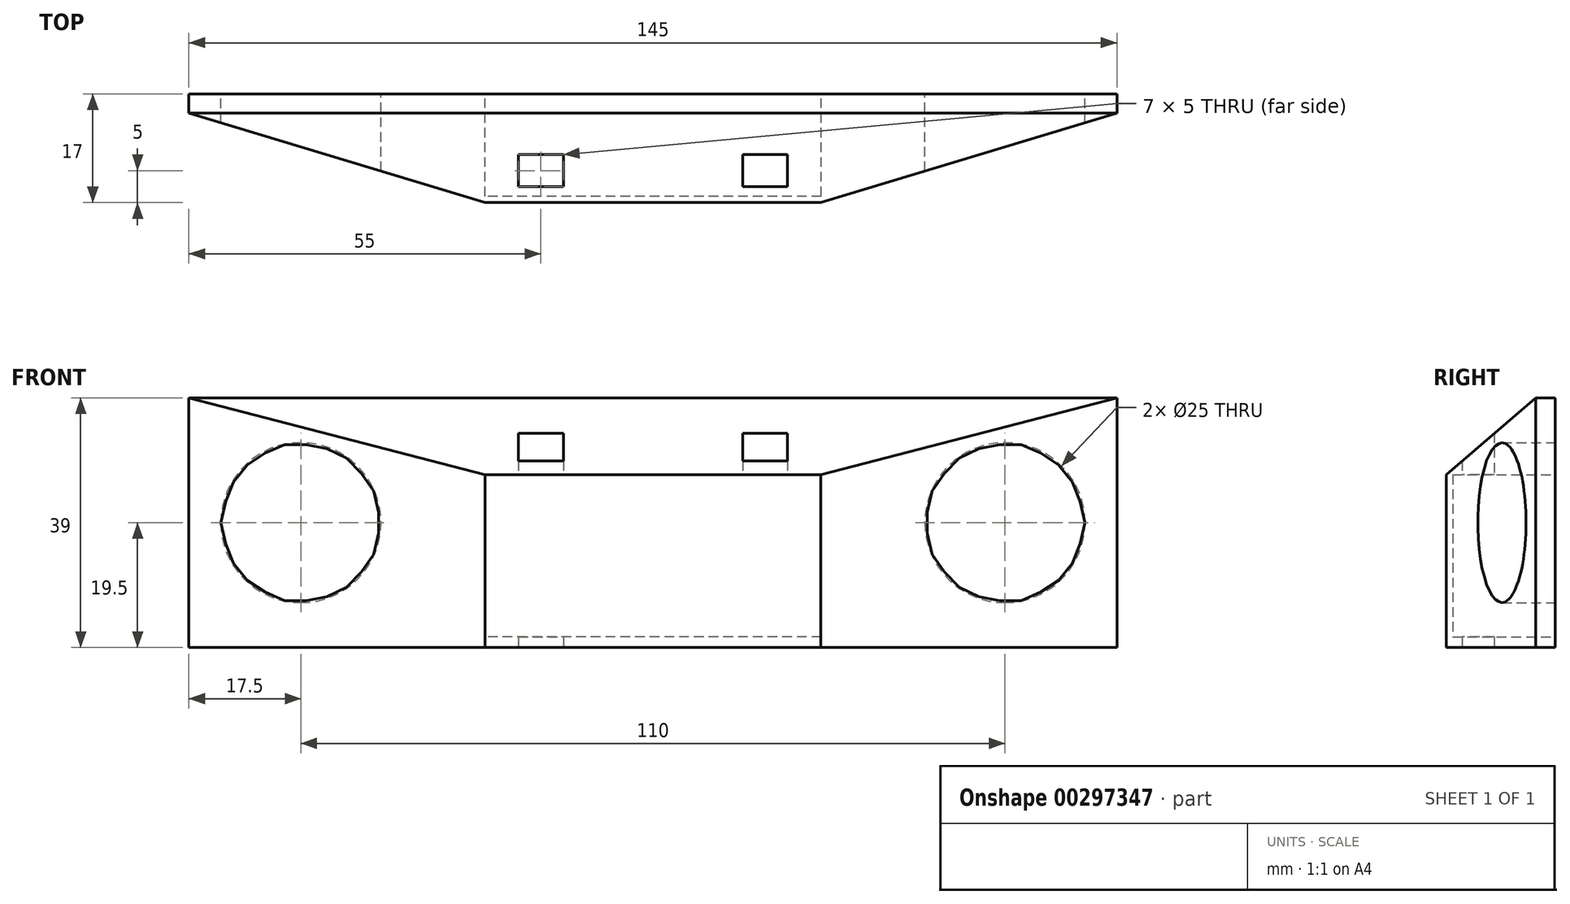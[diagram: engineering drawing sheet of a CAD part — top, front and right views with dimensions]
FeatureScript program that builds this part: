
annotation { "Feature Type Name" : "Feature", "Feature Type Description" : "" }
export const myFeature = defineFeature(function(context is Context, id is Id, definition is map)
    precondition{}
    {
        {
            var Q0;
            Q0=qCreatedBy(makeId("Front.planeOp"),FACE);
            var sketch = newSketch(context, id + "F0", { "sketchPlane" : qUnion([Q0])});
            skLineSegment(sketch, "E0.bottom", {"start": v(72.5, 19.5) * mm, "end": v(-72.5, 19.5) * mm});
            skLineSegment(sketch, "E0.top", {"start": v(72.5, -19.5) * mm, "end": v(-72.5, -19.5) * mm});
            skLineSegment(sketch, "E0.left", {"start": v(72.5, 19.5) * mm, "end": v(72.5, -19.5) * mm});
            skLineSegment(sketch, "E0.right", {"start": v(-72.5, 19.5) * mm, "end": v(-72.5, -19.5) * mm});
            skPoint(sketch, "E0.middle", {"position": v(0, 0) * mm});
            skCircle(sketch, "E1", {"center": v(-55, 0) * mm, "radius": 12.5 * mm});
            skCircle(sketch, "E2", {"center": v(55, 0) * mm, "radius": 12.5 * mm});
            skSolve(sketch);
        }
        {
            var Q0;
            Q0 = qSketchRegion(id + "F0", true);
            extrude(context, id + "F1", {"entities" : qUnion([Q0]), "depth" : 17 * mm});
        }
        {
            var Q0;
            Q0=makeQuery(id+"F1.opExtrude","CAP_FACE",FACE,{"disambiguationData":[OSD([sQuery(id+"F0.wireOp",EDGE,"E0.bottom"),sQuery(id+"F0.wireOp",EDGE,"E0.top"),sQuery(id+"F0.wireOp",EDGE,"E0.left"),sQuery(id+"F0.wireOp",EDGE,"E0.right"),sQuery(id+"F0.wireOp",EDGE,"E1"),sQuery(id+"F0.wireOp",EDGE,"E2")])],"isStart":false});
            var sketch = newSketch(context, id + "F2", { "sketchPlane" : qUnion([Q0])});
            skLineSegment(sketch, "E3.bottom", {"start": v(-26.25, -19.5) * mm, "end": v(26.25, -19.5) * mm, "construction": true});
            skLineSegment(sketch, "E3.top", {"start": v(-26.25, 7.5) * mm, "end": v(26.25, 7.5) * mm, "construction": true});
            skLineSegment(sketch, "E3.left", {"start": v(-26.25, -19.5) * mm, "end": v(-26.25, 7.5) * mm, "construction": true});
            skLineSegment(sketch, "E3.right", {"start": v(26.25, -19.5) * mm, "end": v(26.25, 7.5) * mm, "construction": true});
            skSolve(sketch);
        }
        {
            var Q0;
            Q0=makeQuery(id+"F1.opExtrude","SWEPT_FACE",FACE,{"disambiguationData":[OSD([sQuery(id+"F0.wireOp",EDGE,"E0.right")])]});
            var sketch = newSketch(context, id + "F3", { "sketchPlane" : qUnion([Q0])});
            skLineSegment(sketch, "E4", {"start": v(17, 7.5) * mm, "end": v(3, 19.5) * mm});
            skLineSegment(sketch, "E5", {"start": v(3, 19.5) * mm, "end": v(17, 19.5) * mm});
            skLineSegment(sketch, "E6", {"start": v(17, 19.5) * mm, "end": v(17, 7.5) * mm});
            skSolve(sketch);
        }
        {
            var Q0;
            Q0 = qSketchRegion(id + "F3", true);
            extrude(context, id + "F4", {"entities" : qUnion([Q0]), "operationType" : NewBodyOperationType.REMOVE, "oppositeDirection" : true, "depth" : 300 * mm});
        }
        {
            var Q0;
            Q0=makeQuery(id+"F1.opExtrude","SWEPT_FACE",FACE,{"disambiguationData":[OSD([sQuery(id+"F0.wireOp",EDGE,"E0.top")])]});
            var sketch = newSketch(context, id + "F5", { "sketchPlane" : qUnion([Q0])});
            skLineSegment(sketch, "E7", {"start": v(-26.25, 17) * mm, "end": v(-72.5, 3) * mm});
            skLineSegment(sketch, "E8", {"start": v(-72.5, 3) * mm, "end": v(-72.5, 17) * mm});
            skLineSegment(sketch, "E9", {"start": v(-72.5, 17) * mm, "end": v(-26.25, 17) * mm});
            skLineSegment(sketch, "E10", {"start": v(26.25, 17) * mm, "end": v(72.5, 3) * mm});
            skLineSegment(sketch, "E11", {"start": v(72.5, 3) * mm, "end": v(72.5, 17) * mm});
            skLineSegment(sketch, "E12", {"start": v(72.5, 17) * mm, "end": v(26.25, 17) * mm});
            skSolve(sketch);
        }
        {
            var Q0;
            Q0 = qSketchRegion(id + "F5", true);
            extrude(context, id + "F6", {"entities" : qUnion([Q0]), "operationType" : NewBodyOperationType.REMOVE, "oppositeDirection" : true, "depth" : 100 * mm});
        }
        {
            var Q0;
            Q0=makeQuery(id+"F1.opExtrude","SWEPT_FACE",FACE,{"disambiguationData":[OSD([sQuery(id+"F0.wireOp",EDGE,"E0.top")])]});
            var sketch = newSketch(context, id + "F7", { "sketchPlane" : qUnion([Q0])});
            skLineSegment(sketch, "E13.bottom", {"start": v(17.5, 12) * mm, "end": v(-17.5, 12) * mm, "construction": true});
            skLineSegment(sketch, "E13.top", {"start": v(17.5, 12) * mm, "end": v(-17.5, 12) * mm, "construction": true});
            skLineSegment(sketch, "E13.left", {"start": v(17.5, 12) * mm, "end": v(17.5, 12) * mm});
            skLineSegment(sketch, "E13.right", {"start": v(-17.5, 12) * mm, "end": v(-17.5, 12) * mm});
            skPoint(sketch, "E13.middle", {"position": v(0, 12) * mm});
            skLineSegment(sketch, "E14.bottom", {"start": v(-14, 14.5) * mm, "end": v(-21, 14.5) * mm});
            skLineSegment(sketch, "E14.top", {"start": v(-14, 9.5) * mm, "end": v(-21, 9.5) * mm});
            skLineSegment(sketch, "E14.left", {"start": v(-14, 14.5) * mm, "end": v(-14, 9.5) * mm});
            skLineSegment(sketch, "E14.right", {"start": v(-21, 14.5) * mm, "end": v(-21, 9.5) * mm});
            skPoint(sketch, "E14.middle", {"position": v(-17.5, 12) * mm});
            skLineSegment(sketch, "E15.bottom", {"start": v(21, 14.5) * mm, "end": v(14, 14.5) * mm});
            skLineSegment(sketch, "E15.top", {"start": v(21, 9.5) * mm, "end": v(14, 9.5) * mm});
            skLineSegment(sketch, "E15.left", {"start": v(21, 14.5) * mm, "end": v(21, 9.5) * mm});
            skLineSegment(sketch, "E15.right", {"start": v(14, 14.5) * mm, "end": v(14, 9.5) * mm});
            skPoint(sketch, "E15.middle", {"position": v(17.5, 12) * mm});
            skSolve(sketch);
        }
        {
            var Q0;
            Q0 = qSketchRegion(id + "F7", true);
            extrude(context, id + "F8", {"entities" : qUnion([Q0]), "operationType" : NewBodyOperationType.REMOVE, "oppositeDirection" : true, "depth" : 200 * mm});
        }
        {
            var Q0;
            Q0=makeQuery(id+"F1.opExtrude","SWEPT_FACE",FACE,{"disambiguationData":[OSD([sQuery(id+"F0.wireOp",EDGE,"E0.top")])]});
            var sketch = newSketch(context, id + "F9", { "sketchPlane" : qUnion([Q0])});
            skLineSegment(sketch, "E16.bottom", {"start": v(12.17, 15.76) * mm, "end": v(22.64, 15.76) * mm});
            skLineSegment(sketch, "E16.top", {"start": v(12.17, 8.51) * mm, "end": v(22.64, 8.51) * mm});
            skLineSegment(sketch, "E16.left", {"start": v(12.17, 15.76) * mm, "end": v(12.17, 8.51) * mm});
            skLineSegment(sketch, "E16.right", {"start": v(22.64, 15.76) * mm, "end": v(22.64, 8.51) * mm});
            skSolve(sketch);
        }
        {
            var Q0;
            Q0 = qSketchRegion(id + "F9", true);
            extrude(context, id + "F10", {"entities" : qUnion([Q0]), "operationType" : NewBodyOperationType.ADD, "oppositeDirection" : true, "depth" : 3 * mm});
        }
        {
            var Q0;
            Q0=makeQuery(id+"F1.opExtrude","CAP_FACE",FACE,{"disambiguationData":[OSD([sQuery(id+"F0.wireOp",EDGE,"E0.bottom"),sQuery(id+"F0.wireOp",EDGE,"E0.top"),sQuery(id+"F0.wireOp",EDGE,"E0.left"),sQuery(id+"F0.wireOp",EDGE,"E0.right"),sQuery(id+"F0.wireOp",EDGE,"E1"),sQuery(id+"F0.wireOp",EDGE,"E2")])],"isStart":true});
            var sketch = newSketch(context, id + "F11", { "sketchPlane" : qUnion([Q0])});
            skLineSegment(sketch, "E17.bottom", {"start": v(-26.31, 7.48) * mm, "end": v(26.23, 7.48) * mm});
            skLineSegment(sketch, "E17.top", {"start": v(-26.31, -17.87) * mm, "end": v(26.23, -17.87) * mm});
            skLineSegment(sketch, "E17.left", {"start": v(-26.31, 7.48) * mm, "end": v(-26.31, -17.87) * mm});
            skLineSegment(sketch, "E17.right", {"start": v(26.23, 7.48) * mm, "end": v(26.23, -17.87) * mm});
            skSolve(sketch);
        }
        {
            var Q0;
            Q0 = qSketchRegion(id + "F11", true);
            extrude(context, id + "F12", {"entities" : qUnion([Q0]), "operationType" : NewBodyOperationType.REMOVE, "oppositeDirection" : true, "depth" : 16 * mm});
        }
    });
